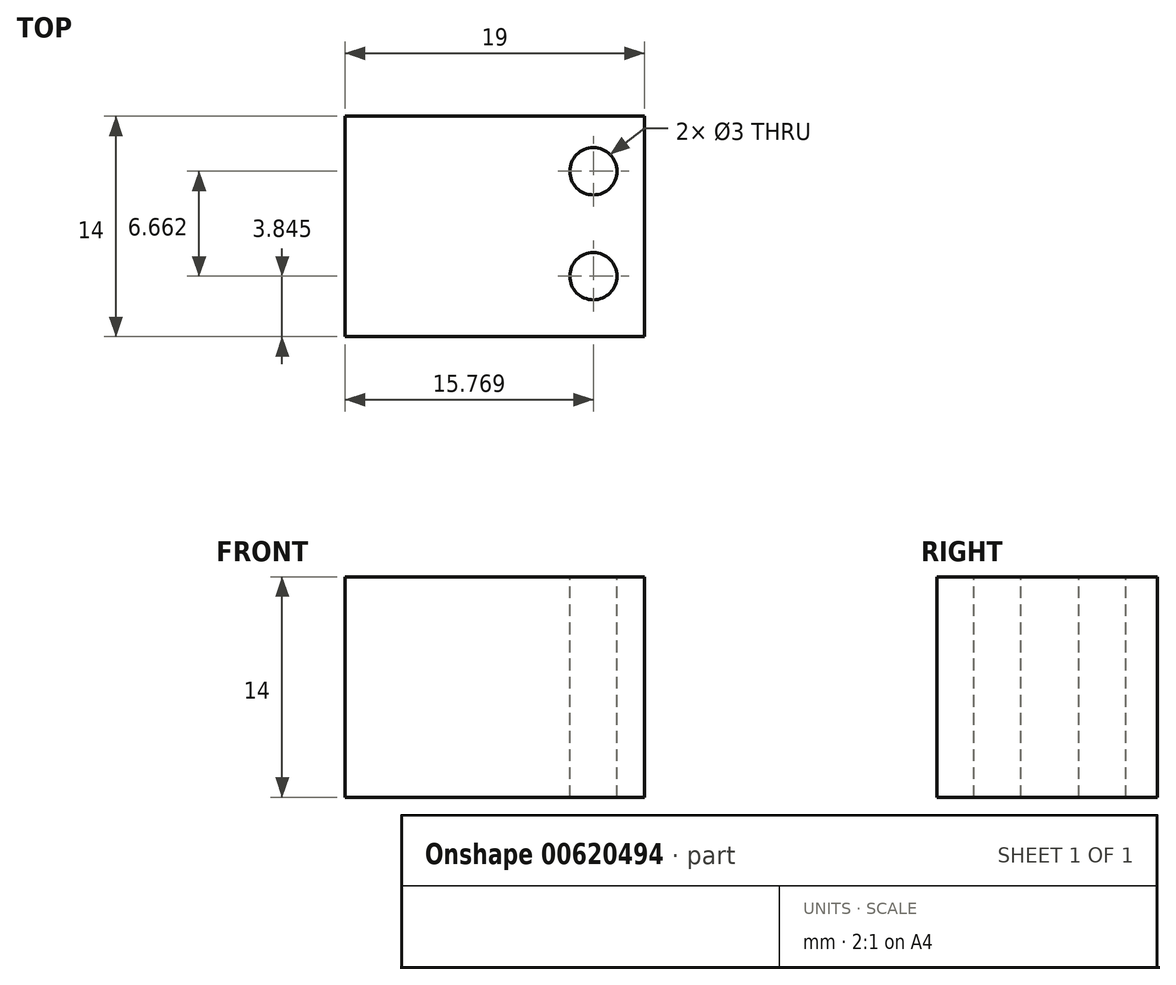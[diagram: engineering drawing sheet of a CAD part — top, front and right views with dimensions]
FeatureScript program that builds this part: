
annotation { "Feature Type Name" : "Feature", "Feature Type Description" : "" }
export const myFeature = defineFeature(function(context is Context, id is Id, definition is map)
    precondition{}
    {
        {
            var Q0;
            Q0=qCreatedBy(makeId("Front.planeOp"),FACE);
            var sketch = newSketch(context, id + "F0", { "sketchPlane" : qUnion([Q0])});
            skLineSegment(sketch, "E0.bottom", {"start": v(0, 0) * mm, "end": v(-19, 0) * mm});
            skLineSegment(sketch, "E0.top", {"start": v(0, 14) * mm, "end": v(-19, 14) * mm});
            skLineSegment(sketch, "E0.left", {"start": v(0, 0) * mm, "end": v(0, 14) * mm});
            skLineSegment(sketch, "E0.right", {"start": v(-19, 0) * mm, "end": v(-19, 14) * mm});
            skSolve(sketch);
        }
        {
            var Q0;
            Q0=makeQuery(id+"F0.imprint","IMPRINT",FACE,{"disambiguationData":[TD([[makeQuery(id+"F0.imprint","IMPRINT",EDGE,{"derivedFrom":sQuery(id+"F0.wireOp",EDGE,"E0.bottom")}),-1.0]])]});
            extrude(context, id + "F1", {"entities" : qUnion([Q0]), "depth" : 14 * mm, "offsetDistance" : 25.4 * mm});
        }
        {
            var Q0;
            Q0=makeQuery(id+"F1.opExtrude","SWEPT_FACE",FACE,{"disambiguationData":[OSD([sQuery(id+"F0.wireOp",EDGE,"E0.top")])]});
            var sketch = newSketch(context, id + "F2", { "sketchPlane" : qUnion([Q0])});
            skCircle(sketch, "E1", {"center": v(-3.23, -10.16) * mm, "radius": 1.5 * mm});
            skCircle(sketch, "E2", {"center": v(-3.23, -3.5) * mm, "radius": 1.5 * mm});
            skSolve(sketch);
        }
        {
            var Q0;
            Q0=makeQuery(id+"F2.imprint","IMPRINT",FACE,{"disambiguationData":[TD([[makeQuery(id+"F2.imprint","IMPRINT",EDGE,{"derivedFrom":sQuery(id+"F2.wireOp",EDGE,"E2")}),1.0]])]});
            var Q1;
            Q1=makeQuery(id+"F2.imprint","IMPRINT",FACE,{"disambiguationData":[TD([[makeQuery(id+"F2.imprint","IMPRINT",EDGE,{"derivedFrom":sQuery(id+"F2.wireOp",EDGE,"E1")}),1.0]])]});
            extrude(context, id + "F3", {"entities" : qUnion([Q0, Q1]), "operationType" : NewBodyOperationType.REMOVE, "oppositeDirection" : true, "depth" : 14 * mm, "offsetDistance" : 25.4 * mm});
        }
    });
